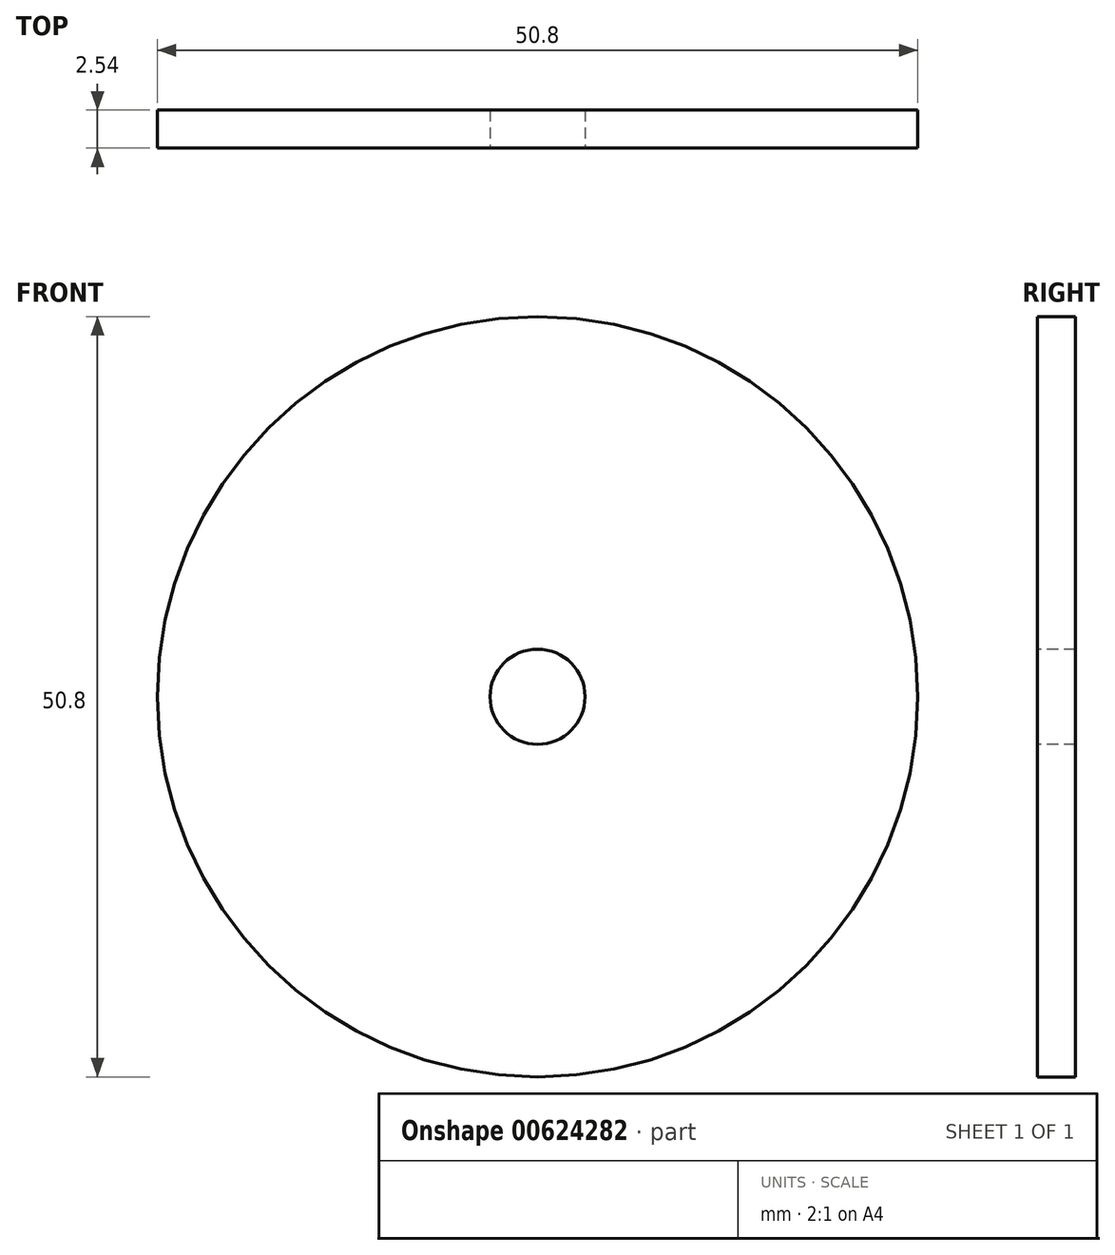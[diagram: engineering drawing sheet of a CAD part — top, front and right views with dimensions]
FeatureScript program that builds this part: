
annotation { "Feature Type Name" : "Feature", "Feature Type Description" : "" }
export const myFeature = defineFeature(function(context is Context, id is Id, definition is map)
    precondition{}
    {
        {
            var Q0;
            Q0=qCreatedBy(makeId("Front.planeOp"),FACE);
            var sketch = newSketch(context, id + "F0", { "sketchPlane" : qUnion([Q0])});
            skCircle(sketch, "E0", {"center": v(0, 0) * mm, "radius": 25.4 * mm});
            skCircle(sketch, "E1", {"center": v(0, 0) * mm, "radius": 3.18 * mm});
            skCircle(sketch, "E2", {"center": v(-50.47, 0) * mm, "radius": 3.18 * mm});
            skCircle(sketch, "E3", {"center": v(48.78, 0) * mm, "radius": 3.18 * mm});
            skCircle(sketch, "E4", {"center": v(0, 53.17) * mm, "radius": 3.18 * mm});
            skCircle(sketch, "E5", {"center": v(0, -53.5) * mm, "radius": 3.18 * mm});
            skSolve(sketch);
        }
        {
            var Q0;
            Q0=sQuery(id+"F0.wireOp",EDGE,"E0");
            var Q1;
            Q1=sQuery(id+"F0.wireOp",EDGE,"E1");
            extrude(context, id + "F1", {"bodyType" : ToolBodyType.SURFACE, "surfaceEntities" : qUnion([Q0, Q1]), "depth" : 2.54 * mm, "offsetDistance" : 25.4 * mm});
        }
    });
